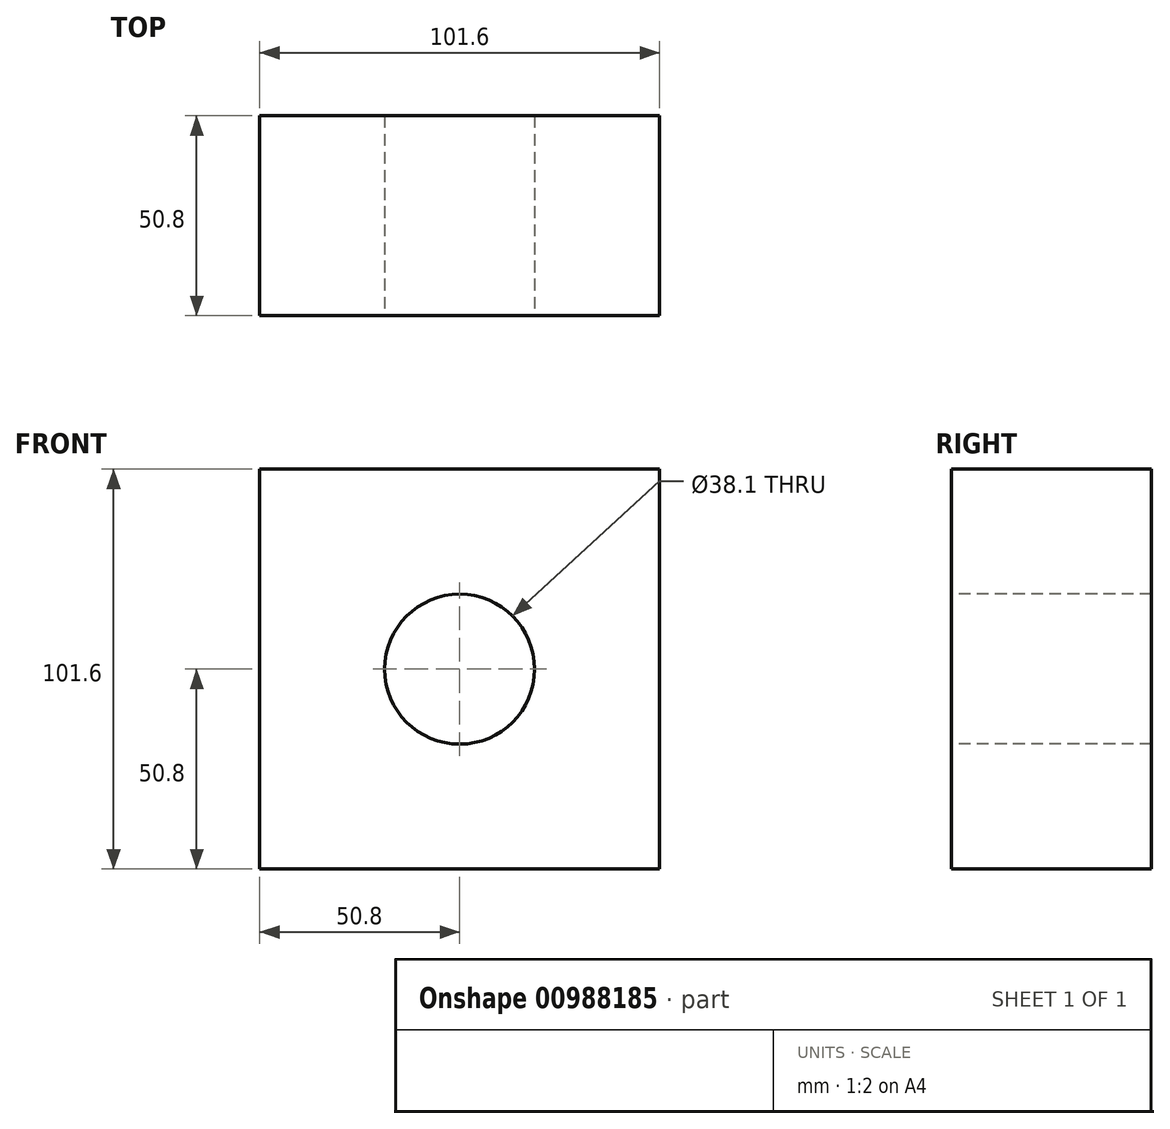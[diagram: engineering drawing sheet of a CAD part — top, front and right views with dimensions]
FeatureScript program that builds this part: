
annotation { "Feature Type Name" : "Feature", "Feature Type Description" : "" }
export const myFeature = defineFeature(function(context is Context, id is Id, definition is map)
    precondition{}
    {
        {
            var Q0;
            Q0=qCreatedBy(makeId("Top.planeOp"),FACE);
            var sketch = newSketch(context, id + "F0", { "sketchPlane" : qUnion([Q0])});
            skLineSegment(sketch, "E0.bottom", {"start": v(50.8, -25.4) * mm, "end": v(-50.8, -25.4) * mm});
            skLineSegment(sketch, "E0.top", {"start": v(50.8, 25.4) * mm, "end": v(-50.8, 25.4) * mm});
            skLineSegment(sketch, "E0.left", {"start": v(50.8, -25.4) * mm, "end": v(50.8, 25.4) * mm});
            skLineSegment(sketch, "E0.right", {"start": v(-50.8, -25.4) * mm, "end": v(-50.8, 25.4) * mm});
            skPoint(sketch, "E0.middle", {"position": v(0, 0) * mm});
            skSolve(sketch);
        }
        {
            var Q0;
            Q0=qSketchRegion(id+"F0",true);
            extrude(context, id + "F1", {"entities" : qUnion([Q0]), "depth" : 101.6 * mm, "offsetDistance" : 25.4 * mm});
        }
        {
            var Q0;
            Q0=makeQuery(id+"F1.opExtrude","SWEPT_FACE",FACE,{"disambiguationData":[OSD([sQuery(id+"F0.wireOp",EDGE,"E0.bottom")])]});
            var sketch = newSketch(context, id + "F2", { "sketchPlane" : qUnion([Q0])});
            skCircle(sketch, "E1", {"center": v(0, 50.8) * mm, "radius": 19.05 * mm});
            skPoint(sketch, "E1.centerSnap0", {"position": v(50.8, 50.8) * mm});
            skSolve(sketch);
        }
        {
            var Q0;
            Q0=makeQuery(id+"F2.imprint","IMPRINT",FACE,{"disambiguationData":[TD([[makeQuery(id+"F2.imprint","IMPRINT",EDGE,{"derivedFrom":sQuery(id+"F2.wireOp",EDGE,"E1")}),1.0]])]});
            extrude(context, id + "F3", {"entities" : qUnion([Q0]), "operationType" : NewBodyOperationType.REMOVE, "endBound" : BoundingType.THROUGH_ALL, "oppositeDirection" : true, "depth" : 25.4 * mm, "offsetDistance" : 25.4 * mm});
        }
    });
